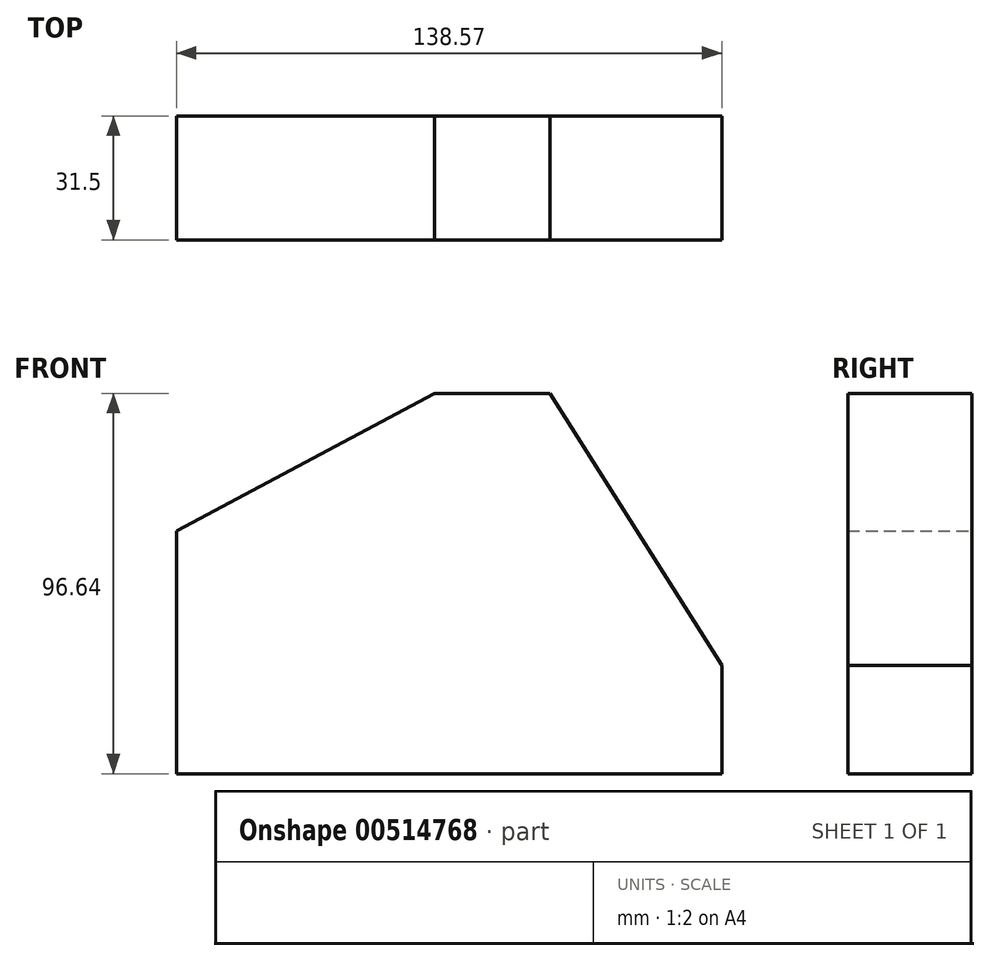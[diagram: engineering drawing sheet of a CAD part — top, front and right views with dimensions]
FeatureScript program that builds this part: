
annotation { "Feature Type Name" : "Feature", "Feature Type Description" : "" }
export const myFeature = defineFeature(function(context is Context, id is Id, definition is map)
    precondition{}
    {
        {
            var Q0;
            Q0=qCreatedBy(makeId("Front.planeOp"),FACE);
            var sketch = newSketch(context, id + "F0", { "sketchPlane" : qUnion([Q0])});
            skLineSegment(sketch, "E0.bottom", {"start": v(-63.62, 49.89) * mm, "end": v(74.95, 49.89) * mm});
            skLineSegment(sketch, "E0.top", {"start": v(-63.62, -46.75) * mm, "end": v(74.95, -46.75) * mm});
            skLineSegment(sketch, "E0.left", {"start": v(-63.62, 49.89) * mm, "end": v(-63.62, -46.75) * mm});
            skLineSegment(sketch, "E0.right", {"start": v(74.95, 49.89) * mm, "end": v(74.95, -46.75) * mm});
            skLineSegment(sketch, "E1", {"start": v(-63.62, 14.94) * mm, "end": v(1.93, 49.89) * mm});
            skLineSegment(sketch, "E2", {"start": v(31.33, 49.89) * mm, "end": v(74.95, -19.28) * mm});
            skSolve(sketch);
        }
        {
            var Q0;
            {var subQ1=sQuery(id+"F0.wireOp",EDGE,"E0.top");Q0=makeQuery(id+"F0.imprint","IMPRINT",FACE,{"disambiguationData":[TD([[makeQuery(id+"F0.imprint","IMPRINT",EDGE,{"derivedFrom":subQ1}),1.0]])]});}
            extrude(context, id + "F1", {"entities" : qUnion([Q0]), "depth" : 31.5 * mm, "offsetDistance" : 25.4 * mm});
        }
    });
